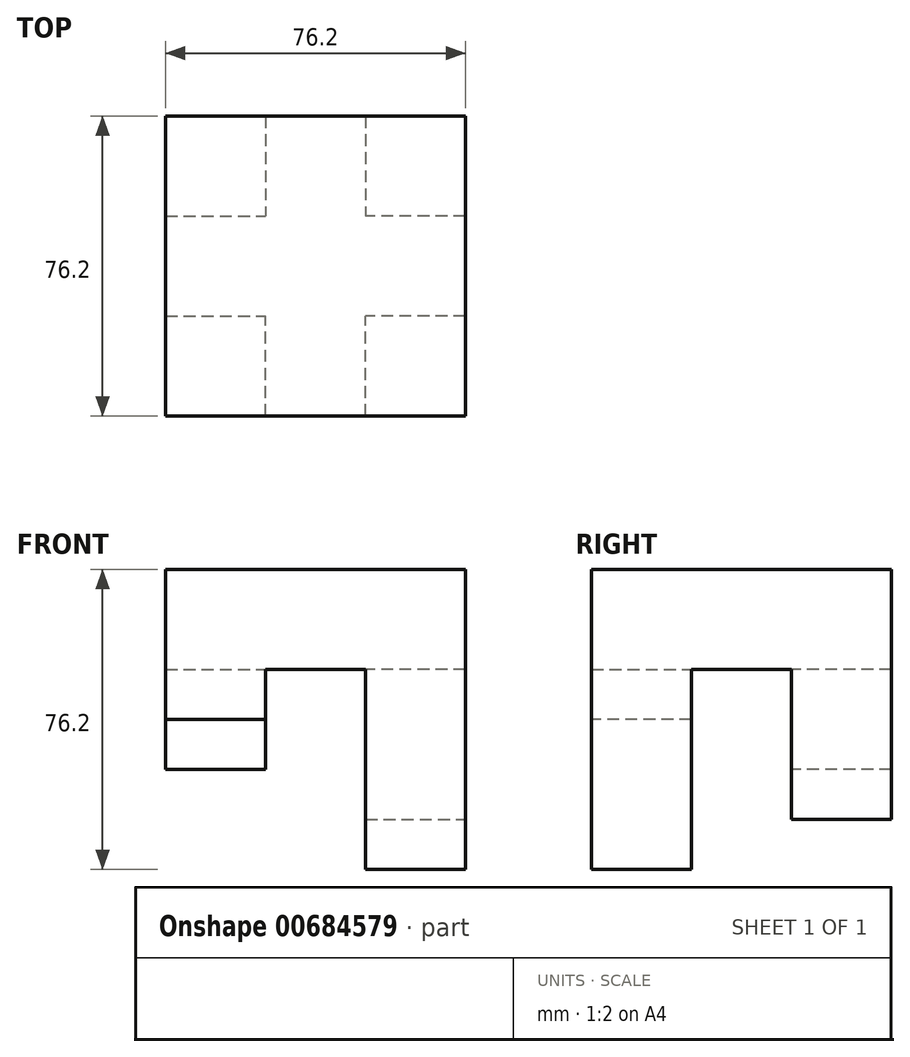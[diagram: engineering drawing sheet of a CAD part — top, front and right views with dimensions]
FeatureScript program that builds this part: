
annotation { "Feature Type Name" : "Feature", "Feature Type Description" : "" }
export const myFeature = defineFeature(function(context is Context, id is Id, definition is map)
    precondition{}
    {
        {
            var Q0;
            Q0=qCreatedBy(makeId("Top.planeOp"),FACE);
            var sketch = newSketch(context, id + "F0", { "sketchPlane" : qUnion([Q0])});
            skLineSegment(sketch, "E0.bottom", {"start": v(-45.31, 55.73) * mm, "end": v(30.89, 55.73) * mm});
            skLineSegment(sketch, "E0.top", {"start": v(-45.31, -20.47) * mm, "end": v(30.89, -20.47) * mm});
            skLineSegment(sketch, "E0.left", {"start": v(-45.31, 55.73) * mm, "end": v(-45.31, -20.47) * mm});
            skLineSegment(sketch, "E0.right", {"start": v(30.89, 55.73) * mm, "end": v(30.89, -20.47) * mm});
            skSolve(sketch);
        }
        {
            var Q0;
            Q0=makeQuery(id+"F0.imprint","IMPRINT",FACE,{"disambiguationData":[TD([[makeQuery(id+"F0.imprint","IMPRINT",EDGE,{"derivedFrom":sQuery(id+"F0.wireOp",EDGE,"E0.bottom")}),-1.0]])]});
            extrude(context, id + "F1", {"entities" : qUnion([Q0]), "depth" : 25.4 * mm, "offsetDistance" : 25.4 * mm});
        }
        {
            var Q0;
            Q0=makeQuery(id+"F1.opExtrude","CAP_FACE",FACE,{"disambiguationData":[OSD([sQuery(id+"F0.wireOp",EDGE,"E0.bottom"),sQuery(id+"F0.wireOp",EDGE,"E0.top"),sQuery(id+"F0.wireOp",EDGE,"E0.left"),sQuery(id+"F0.wireOp",EDGE,"E0.right")])],"isStart":true});
            var sketch = newSketch(context, id + "F2", { "sketchPlane" : qUnion([Q0])});
            skLineSegment(sketch, "E1.bottom", {"start": v(-45.31, -55.73) * mm, "end": v(-19.91, -55.73) * mm});
            skLineSegment(sketch, "E1.top", {"start": v(-45.31, -30.33) * mm, "end": v(-19.91, -30.33) * mm});
            skLineSegment(sketch, "E1.left", {"start": v(-45.31, -55.73) * mm, "end": v(-45.31, -30.33) * mm});
            skLineSegment(sketch, "E1.right", {"start": v(-19.91, -55.73) * mm, "end": v(-19.91, -30.33) * mm});
            skSolve(sketch);
        }
        {
            var Q0;
            Q0=makeQuery(id+"F2.imprint","IMPRINT",FACE,{"disambiguationData":[TD([[makeQuery(id+"F2.imprint","IMPRINT",EDGE,{"derivedFrom":sQuery(id+"F2.wireOp",EDGE,"E1.bottom")}),1.0]])]});
            extrude(context, id + "F3", {"entities" : qUnion([Q0]), "operationType" : NewBodyOperationType.ADD, "depth" : 25.4 * mm, "offsetDistance" : 25.4 * mm});
        }
        {
            var Q0;
            Q0=makeQuery(id+"F1.opExtrude","CAP_FACE",FACE,{"disambiguationData":[OSD([sQuery(id+"F0.wireOp",EDGE,"E0.bottom"),sQuery(id+"F0.wireOp",EDGE,"E0.top"),sQuery(id+"F0.wireOp",EDGE,"E0.left"),sQuery(id+"F0.wireOp",EDGE,"E0.right")])],"isStart":true});
            var sketch = newSketch(context, id + "F4", { "sketchPlane" : qUnion([Q0])});
            skLineSegment(sketch, "E2.bottom", {"start": v(-45.31, 20.47) * mm, "end": v(-19.91, 20.47) * mm});
            skLineSegment(sketch, "E2.top", {"start": v(-45.31, -4.93) * mm, "end": v(-19.91, -4.93) * mm});
            skLineSegment(sketch, "E2.left", {"start": v(-45.31, 20.47) * mm, "end": v(-45.31, -4.93) * mm});
            skLineSegment(sketch, "E2.right", {"start": v(-19.91, 20.47) * mm, "end": v(-19.91, -4.93) * mm});
            skSolve(sketch);
        }
        {
            var Q0;
            Q0=makeQuery(id+"F4.imprint","IMPRINT",FACE,{"disambiguationData":[TD([[makeQuery(id+"F4.imprint","IMPRINT",EDGE,{"derivedFrom":sQuery(id+"F4.wireOp",EDGE,"E2.bottom")}),-1.0]])]});
            extrude(context, id + "F5", {"entities" : qUnion([Q0]), "operationType" : NewBodyOperationType.ADD, "depth" : 12.7 * mm, "offsetDistance" : 25.4 * mm});
        }
        {
            var Q0;
            Q0=makeQuery(id+"F1.opExtrude","CAP_FACE",FACE,{"disambiguationData":[OSD([sQuery(id+"F0.wireOp",EDGE,"E0.bottom"),sQuery(id+"F0.wireOp",EDGE,"E0.top"),sQuery(id+"F0.wireOp",EDGE,"E0.left"),sQuery(id+"F0.wireOp",EDGE,"E0.right")])],"isStart":true});
            var sketch = newSketch(context, id + "F6", { "sketchPlane" : qUnion([Q0])});
            skLineSegment(sketch, "E3.bottom", {"start": v(30.89, 20.47) * mm, "end": v(5.49, 20.47) * mm});
            skLineSegment(sketch, "E3.top", {"start": v(30.89, -4.93) * mm, "end": v(5.49, -4.93) * mm});
            skLineSegment(sketch, "E3.left", {"start": v(30.89, 20.47) * mm, "end": v(30.89, -4.93) * mm});
            skLineSegment(sketch, "E3.right", {"start": v(5.49, 20.47) * mm, "end": v(5.49, -4.93) * mm});
            skSolve(sketch);
        }
        {
            var Q0;
            Q0=makeQuery(id+"F6.imprint","IMPRINT",FACE,{"disambiguationData":[TD([[makeQuery(id+"F6.imprint","IMPRINT",EDGE,{"derivedFrom":sQuery(id+"F6.wireOp",EDGE,"E3.bottom")}),-1.0]])]});
            extrude(context, id + "F7", {"entities" : qUnion([Q0]), "operationType" : NewBodyOperationType.ADD, "depth" : 50.8 * mm, "offsetDistance" : 25.4 * mm});
        }
        {
            var Q0;
            Q0=makeQuery(id+"F1.opExtrude","CAP_FACE",FACE,{"disambiguationData":[OSD([sQuery(id+"F0.wireOp",EDGE,"E0.bottom"),sQuery(id+"F0.wireOp",EDGE,"E0.top"),sQuery(id+"F0.wireOp",EDGE,"E0.left"),sQuery(id+"F0.wireOp",EDGE,"E0.right")])],"isStart":true});
            var sketch = newSketch(context, id + "F8", { "sketchPlane" : qUnion([Q0])});
            skLineSegment(sketch, "E4.bottom", {"start": v(30.89, -55.73) * mm, "end": v(5.49, -55.73) * mm});
            skLineSegment(sketch, "E4.top", {"start": v(30.89, -30.33) * mm, "end": v(5.49, -30.33) * mm});
            skLineSegment(sketch, "E4.left", {"start": v(30.89, -55.73) * mm, "end": v(30.89, -30.33) * mm});
            skLineSegment(sketch, "E4.right", {"start": v(5.49, -55.73) * mm, "end": v(5.49, -30.33) * mm});
            skSolve(sketch);
        }
        {
            var Q0;
            Q0=makeQuery(id+"F8.imprint","IMPRINT",FACE,{"disambiguationData":[TD([[makeQuery(id+"F8.imprint","IMPRINT",EDGE,{"derivedFrom":sQuery(id+"F8.wireOp",EDGE,"E4.bottom")}),1.0]])]});
            extrude(context, id + "F9", {"entities" : qUnion([Q0]), "operationType" : NewBodyOperationType.ADD, "depth" : 38.1 * mm, "offsetDistance" : 25.4 * mm});
        }
    });
